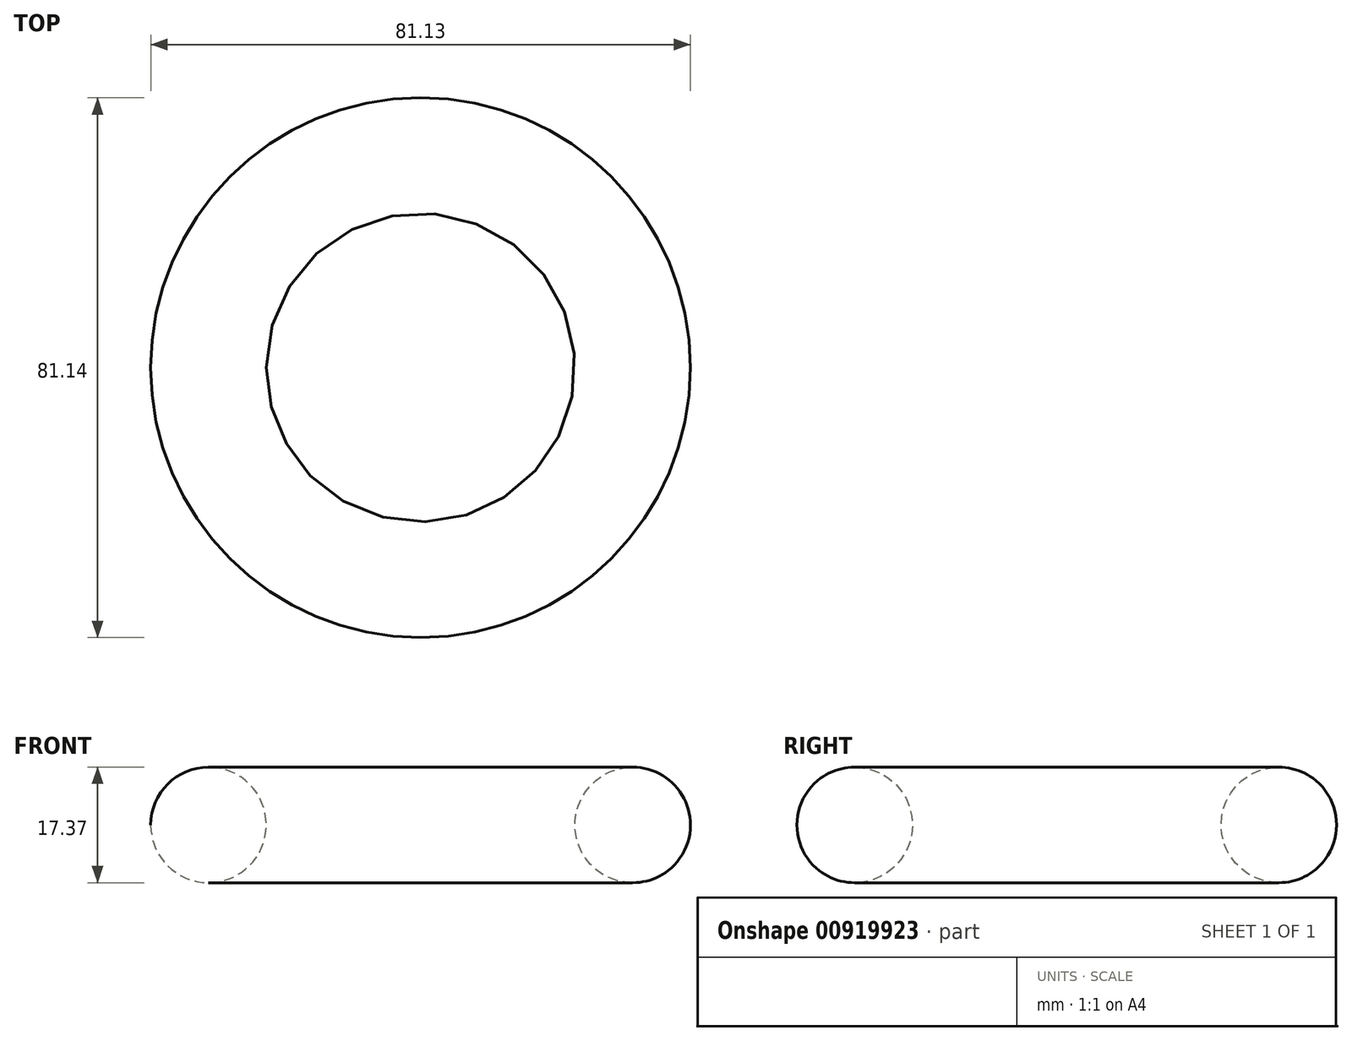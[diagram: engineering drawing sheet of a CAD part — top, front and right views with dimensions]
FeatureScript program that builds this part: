
annotation { "Feature Type Name" : "Feature", "Feature Type Description" : "" }
export const myFeature = defineFeature(function(context is Context, id is Id, definition is map)
    precondition{}
    {
        {
            var Q0;
            Q0=qCreatedBy(makeId("Front.planeOp"),FACE);
            var sketch = newSketch(context, id + "F0", { "sketchPlane" : qUnion([Q0])});
            skLineSegment(sketch, "E0", {"start": v(-5.95, -57.03) * mm, "end": v(-5.95, 66.37) * mm});
            skCircle(sketch, "E1", {"center": v(25.94, 9.81) * mm, "radius": 8.69 * mm});
            skSolve(sketch);
        }
        {
            var Q0;
            Q0 = qSketchRegion(id + "F0", true);
            var Q1;
            Q1=sQuery(id+"F0.wireOp",EDGE,"E0");
            revolve(context, id + "F1", {"surfaceOperationType" : NewSurfaceOperationType.NEW, "entities" : qUnion([Q0]), "axis" : qUnion([Q1]), "revolveType" : RevolveType.FULL});
        }
        {
            var Q0;
            Q0=qCreatedBy(makeId("Front.planeOp"),FACE);
            var sketch = newSketch(context, id + "F2", { "sketchPlane" : qUnion([Q0])});
            skCircle(sketch, "E2", {"center": v(18.52, -23.01) * mm, "radius": 7.9 * mm});
            skSolve(sketch);
        }
        {
            var Q0;
            Q0=makeQuery(id+"F2.imprint","IMPRINT",FACE,{"disambiguationData":[TD([[makeQuery(id+"F2.imprint","IMPRINT",EDGE,{"derivedFrom":sQuery(id+"F2.wireOp",EDGE,"E2")}),1.0]])]});
            cPlane(context, id + "F3", {"entities" : qUnion([Q0]), "cplaneType" : CPlaneType.OFFSET, "offset" : 25.4 * mm, "width" : 152.4 * mm, "height" : 152.4 * mm});
        }
    });
